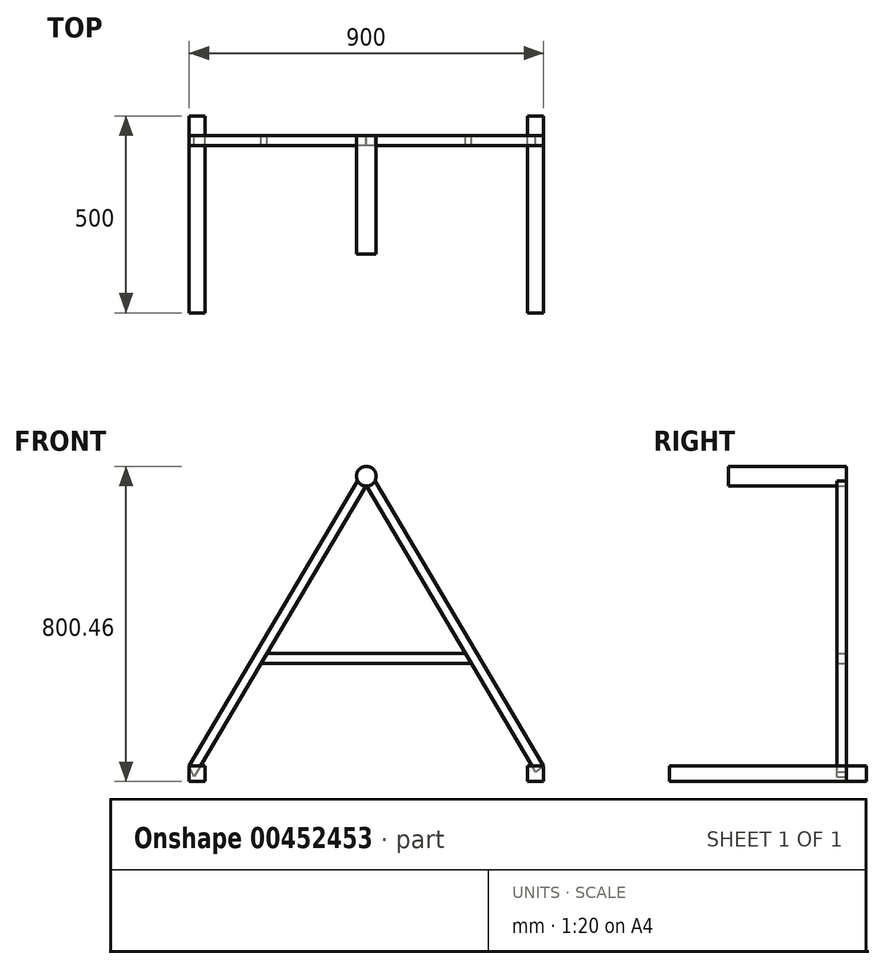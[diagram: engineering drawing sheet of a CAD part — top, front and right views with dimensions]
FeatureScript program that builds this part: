
annotation { "Feature Type Name" : "Feature", "Feature Type Description" : "" }
export const myFeature = defineFeature(function(context is Context, id is Id, definition is map)
    precondition{}
    {
        {
            var Q0;
            Q0=qCreatedBy(makeId("Front.planeOp"),FACE);
            var sketch = newSketch(context, id + "F0", { "sketchPlane" : qUnion([Q0])});
            skLineSegment(sketch, "E0.bottom", {"start": v(-450, -102.98) * mm, "end": v(-410, -102.98) * mm});
            skLineSegment(sketch, "E0.top", {"start": v(-450, -142.98) * mm, "end": v(-410, -142.98) * mm});
            skLineSegment(sketch, "E0.left", {"start": v(-450, -102.98) * mm, "end": v(-450, -142.98) * mm});
            skLineSegment(sketch, "E0.right", {"start": v(-410, -102.98) * mm, "end": v(-410, -142.98) * mm});
            skLineSegment(sketch, "E1.bottom", {"start": v(410, -142.98) * mm, "end": v(450, -142.98) * mm});
            skLineSegment(sketch, "E1.top", {"start": v(410, -102.98) * mm, "end": v(450, -102.98) * mm});
            skLineSegment(sketch, "E1.left", {"start": v(410, -142.98) * mm, "end": v(410, -102.98) * mm});
            skLineSegment(sketch, "E1.right", {"start": v(450, -142.98) * mm, "end": v(450, -102.98) * mm});
            skSolve(sketch);
        }
        {
            var Q0;
            Q0 = qSketchRegion(id + "F0", true);
            extrude(context, id + "F1", {"entities" : qUnion([Q0]), "depth" : 450 * mm});
        }
        {
            var Q0;
            Q0=makeQuery(id+"F1.opExtrude","CAP_FACE",FACE,{"disambiguationData":[OSD([sQuery(id+"F0.wireOp",EDGE,"E1.bottom"),sQuery(id+"F0.wireOp",EDGE,"E1.top"),sQuery(id+"F0.wireOp",EDGE,"E1.left"),sQuery(id+"F0.wireOp",EDGE,"E1.right")])],"isStart":true});
            var sketch = newSketch(context, id + "F2", { "sketchPlane" : qUnion([Q0])});
            skLineSegment(sketch, "E2", {"start": v(-450, -102.98) * mm, "end": v(0, 657.02) * mm});
            skLineSegment(sketch, "E3", {"start": v(0, 657.02) * mm, "end": v(450, -102.98) * mm});
            skLineSegment(sketch, "E4", {"start": v(-430, -118.29) * mm, "end": v(0, 607.95) * mm});
            skLineSegment(sketch, "E5", {"start": v(0, 607.95) * mm, "end": v(437.52, -130.97) * mm});
            skLineSegment(sketch, "E6", {"start": v(-430, -118.29) * mm, "end": v(-450, -102.98) * mm});
            skLineSegment(sketch, "E7", {"start": v(437.52, -130.97) * mm, "end": v(450, -102.98) * mm});
            skSolve(sketch);
        }
        {
            var Q0;
            Q0 = qSketchRegion(id + "F2", true);
            extrude(context, id + "F3", {"entities" : qUnion([Q0]), "oppositeDirection" : true, "depth" : 25 * mm});
        }
        {
            var Q0;
            Q0=makeQuery(id+"F3.opExtrude","CAP_FACE",FACE,{"disambiguationData":[OSD([sQuery(id+"F2.wireOp",EDGE,"E2"),sQuery(id+"F2.wireOp",EDGE,"E3"),sQuery(id+"F2.wireOp",EDGE,"E4"),sQuery(id+"F2.wireOp",EDGE,"E5"),sQuery(id+"F2.wireOp",EDGE,"E6"),sQuery(id+"F2.wireOp",EDGE,"E7")])],"isStart":true});
            var sketch = newSketch(context, id + "F4", { "sketchPlane" : qUnion([Q0])});
            skLineSegment(sketch, "E8", {"start": v(0, 657.02) * mm, "end": v(0, 607.95) * mm, "construction": true});
            skCircle(sketch, "E9", {"center": v(0, 632.48) * mm, "radius": 25 * mm});
            skSolve(sketch);
        }
        {
            var Q0;
            Q0 = qSketchRegion(id + "F4", true);
            extrude(context, id + "F5", {"entities" : qUnion([Q0]), "operationType" : NewBodyOperationType.ADD, "oppositeDirection" : true, "depth" : 300 * mm});
        }
        {
            var Q0;
            Q0 = qSketchRegion(id + "F0", true);
            extrude(context, id + "F6", {"entities" : qUnion([Q0]), "oppositeDirection" : true, "depth" : 50 * mm});
        }
        {
            var Q0;
            Q0=makeQuery(id+"F5.boolean.opBoolean","MERGE",FACE,{"derivedFrom":[makeQuery(id+"F3.opExtrude","CAP_FACE",FACE,{"disambiguationData":[OSD([sQuery(id+"F2.wireOp",EDGE,"E2"),sQuery(id+"F2.wireOp",EDGE,"E3"),sQuery(id+"F2.wireOp",EDGE,"E4"),sQuery(id+"F2.wireOp",EDGE,"E5"),sQuery(id+"F2.wireOp",EDGE,"E6"),sQuery(id+"F2.wireOp",EDGE,"E7")])],"isStart":true}),makeQuery(id+"F5.opExtrude","CAP_FACE",FACE,{"disambiguationData":[OSD([sQuery(id+"F4.wireOp",EDGE,"E9")])],"isStart":true})]});
            var sketch = newSketch(context, id + "F7", { "sketchPlane" : qUnion([Q0])});
            skLineSegment(sketch, "E10", {"start": v(-267, 157.02) * mm, "end": v(267, 157.02) * mm});
            skLineSegment(sketch, "E11", {"start": v(-252.2, 182.02) * mm, "end": v(252.2, 182.02) * mm});
            skLineSegment(sketch, "E12", {"start": v(-267, 157.02) * mm, "end": v(-252.2, 182.02) * mm});
            skLineSegment(sketch, "E13", {"start": v(252.2, 182.02) * mm, "end": v(267, 157.02) * mm});
            skSolve(sketch);
        }
        {
            var Q0;
            Q0 = qSketchRegion(id + "F7", true);
            extrude(context, id + "F8", {"entities" : qUnion([Q0]), "oppositeDirection" : true, "depth" : 25 * mm});
        }
    });
